# Revit family: TOwel_Bar-American_Standard-CR_Series-8336_Series
name_source: partatom
category: Specialty Equipment
units: mm (PartAtom-declared; Revit-internal decimal feet)

## family parameters
Cut with Voids When Loaded = No
Host = Face
OmniClass Number = 23.40.20.21.27
OmniClass Title = Towel Bars
Part Type = Normal
Room Calculation Point = No
Round Connector Dimension = Use Diameter
Shared = Yes

## types (2) — shared parameters
Assembly Code = C1030220
Default Elevation = 40"
Finish = Metal-American Standard-002-Polished Chrome
Height = 2"
Installation Type = Wall Mounted
Length = 4 3/8"
Manufacturer = American Standard
Material = Metal-American Standard-002-Polished Chrome
Price = Prices may vary. Please consult Manufacturer Representative for most up-to-date price list.
Product Documentation Link = https://www.americanstandard-us.com
Product Page URL = https://www.americanstandard-us.com
Revised Date = 04/01/2021
URL = http://www.americanstandard-us.com
Warranty Information = 1 Year Warranty

## per-type parameters (varying)
| type | Description | Installation Instruction Link | Width |
| 8336.018 | CR Series 18" Towel Bar. |  | 18" |
| 8336.024 | CR Series 24" Towel Bar. | https://www.americanstandard-us.com | 24" |

note: column(s) folded — value = type name in every type: Model

## geometry (parser evidence)
native form markers: Sweep x3
no freeform markers — native parametric forms only
